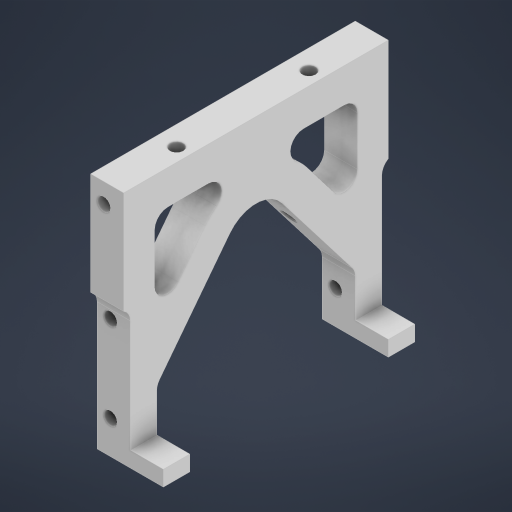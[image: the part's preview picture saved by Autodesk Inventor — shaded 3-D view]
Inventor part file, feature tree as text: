
AUTODESK INVENTOR PART (.ipt)
format: ipt  version: 2024 (Build 280153000, 153)  size: 346,624 bytes
history: native  units: mm
features: extrude x7, sketch x7, fillet x3, other x1, projected_geometry x1
ambient origin geometry x8: Origin, YZ Plane, XZ Plane, XY Plane, X Axis, Y Axis, Z Axis, Center Point
bodies: Body1 (feature_tree)
feature tree (19):
  other  "Твердое тело1"
  extrude  "Выдавливание1"  Depth=2.0mm
  fillet  "Сопряжение1"  Radius=2.0mm
  fillet  "Сопряжение3"  Radius=2.0mm
  sketch  "Эскиз2"
  sketch  "Эскиз3"
  extrude  "Выдавливание2"  Depth=2.0mm
  extrude  "Выдавливание3"  Depth=10.0mm
  extrude  "Выдавливание4"  Depth=10.0mm
  extrude  "Выдавливание5"  Depth=10.0mm
  fillet  "Сопряжение4"  Radius=40.0mm
  extrude  "Выдавливание6"  Depth=76.0mm
  extrude  "Extrusion7"  Depth=10.0mm
  sketch  "Эскиз1"
  sketch  "Эскиз4"
  projected_geometry  "Спроецированная петля1"
  sketch  "Эскиз5"
  sketch  "Эскиз6"
  sketch  "Sketch7"  dims[d0=80.0mm d1=2.0mm d2=2.0mm d3=2.0mm d4=2.0mm d5=44.0mm d6=44.0mm d7=40.0mm d8=40.0mm d9=76.0mm d10=10.0mm d11=10.0mm d12=10.0mm d13=0.0mm d14=10.0mm d16=4.0mm d17=100.0mm d18=0.0mm d19=20.0mm d20=0.0mm d21=22.0mm d22=0.0mm d23=30.0mm d24=30.0mm d25=10.0mm d26=0.0mm d27=4.0mm d28=10.0mm d29=0.0mm d30=1.0mm d31=0.0mm]
